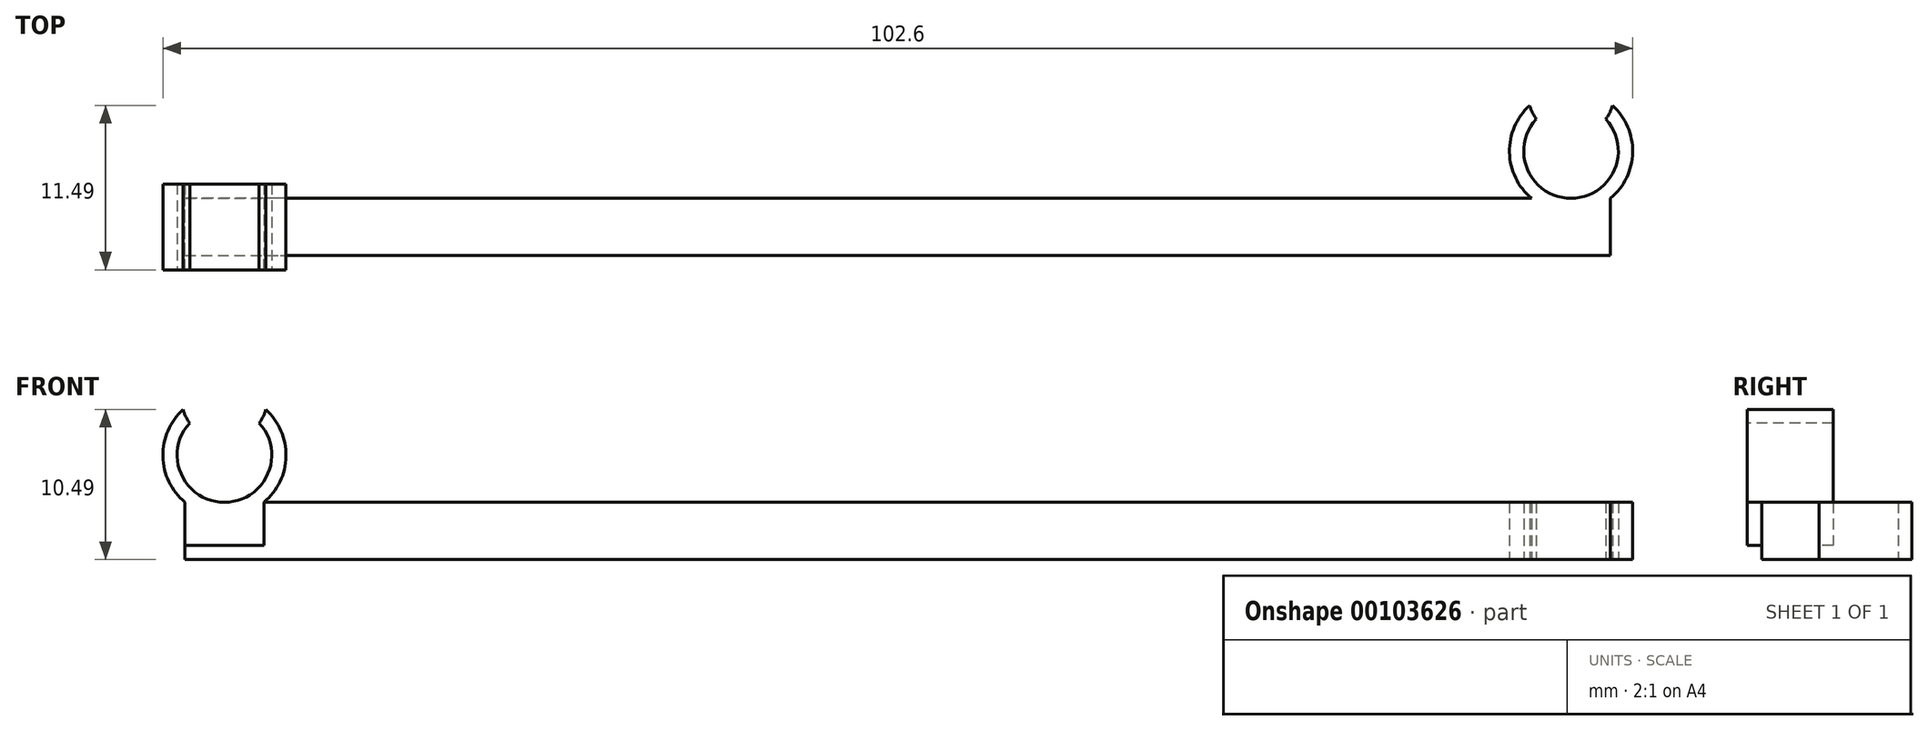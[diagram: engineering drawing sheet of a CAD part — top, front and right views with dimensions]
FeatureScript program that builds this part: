
annotation { "Feature Type Name" : "Feature", "Feature Type Description" : "" }
export const myFeature = defineFeature(function(context is Context, id is Id, definition is map)
    precondition{}
    {
        {
            var Q0;
            Q0=qCreatedBy(makeId("Top.planeOp"),FACE);
            var sketch = newSketch(context, id + "F0", { "sketchPlane" : qUnion([Q0])});
            skArc(sketch, "E0", {"start": v(-2.43, 2.24) * mm, "mid": v(0, -3.3) * mm, "end": v(2.43, 2.24) * mm});
            skArc(sketch, "E1", {"start": v(-2.89, 3.19) * mm, "mid": v(-4.3, -0.09) * mm, "end": v(-2.76, -3.3) * mm});
            skArc(sketch, "E2", {"start": v(-2.89, 3.19) * mm, "mid": v(-2.7, 2.7) * mm, "end": v(-2.43, 2.24) * mm});
            skArc(sketch, "E3.trimOffspring", {"start": v(2.43, 2.24) * mm, "mid": v(2.7, 2.7) * mm, "end": v(2.89, 3.19) * mm});
            skLineSegment(sketch, "E4.bottom", {"start": v(-2.76, -7.3) * mm, "end": v(2.76, -7.3) * mm});
            skLineSegment(sketch, "E4.top", {"start": v(-2.76, -3.3) * mm, "end": v(2.76, -3.3) * mm, "construction": true});
            skLineSegment(sketch, "E4.left", {"start": v(-2.76, -7.3) * mm, "end": v(-2.76, -3.3) * mm});
            skLineSegment(sketch, "E4.right", {"start": v(2.76, -7.3) * mm, "end": v(2.76, -3.3) * mm});
            skArc(sketch, "E5", {"start": v(-2.76, -3.3) * mm, "mid": v(0, -4.3) * mm, "end": v(2.76, -3.3) * mm, "construction": true});
            skArc(sketch, "E6", {"start": v(2.76, -3.3) * mm, "mid": v(4.3, -0.09) * mm, "end": v(2.89, 3.19) * mm});
            skLineSegment(sketch, "E7.bottom", {"start": v(-2.76, -7.3) * mm, "end": v(-96.76, -7.3) * mm});
            skLineSegment(sketch, "E7.top", {"start": v(-2.76, -3.3) * mm, "end": v(-96.76, -3.3) * mm});
            skLineSegment(sketch, "E7.right", {"start": v(-96.76, -7.3) * mm, "end": v(-96.76, -3.3) * mm});
            skSolve(sketch);
        }
        {
            var Q0;
            Q0=qSketchRegion(id+"F0",true);
            extrude(context, id + "F1", {"entities" : qUnion([Q0]), "depth" : 4 * mm});
        }
        {
            var Q0;
            Q0=makeQuery(id+"F1.opExtrude","SWEPT_FACE",FACE,{"disambiguationData":[OSD([sQuery(id+"F0.wireOp",EDGE,"E4.bottom"),sQuery(id+"F0.wireOp",EDGE,"E7.bottom")])]});
            var sketch = newSketch(context, id + "F2", { "sketchPlane" : qUnion([Q0])});
            skArc(sketch, "E8", {"start": v(-96.43, 9.54) * mm, "mid": v(-94, 4) * mm, "end": v(-91.57, 9.54) * mm});
            skArc(sketch, "E9", {"start": v(-96.89, 10.49) * mm, "mid": v(-98.3, 7.21) * mm, "end": v(-96.76, 4) * mm});
            skArc(sketch, "E10", {"start": v(-96.89, 10.49) * mm, "mid": v(-96.7, 10) * mm, "end": v(-96.43, 9.54) * mm});
            skArc(sketch, "E11.trimOffspring", {"start": v(-91.57, 9.54) * mm, "mid": v(-91.3, 10) * mm, "end": v(-91.11, 10.49) * mm});
            skLineSegment(sketch, "E12.bottom", {"start": v(-96.76, 1) * mm, "end": v(-91.24, 1) * mm});
            skLineSegment(sketch, "E12.top", {"start": v(-96.76, 4) * mm, "end": v(-91.24, 4) * mm, "construction": true});
            skLineSegment(sketch, "E12.left", {"start": v(-96.76, 1) * mm, "end": v(-96.76, 4) * mm});
            skLineSegment(sketch, "E12.right", {"start": v(-91.24, 1) * mm, "end": v(-91.24, 4) * mm});
            skArc(sketch, "E13", {"start": v(-96.76, 4) * mm, "mid": v(-94, 3) * mm, "end": v(-91.24, 4) * mm, "construction": true});
            skArc(sketch, "E14", {"start": v(-91.24, 4) * mm, "mid": v(-89.7, 7.21) * mm, "end": v(-91.11, 10.49) * mm});
            skSolve(sketch);
        }
        {
            var Q0;
            Q0 = qSketchRegion(id + "F2", true);
            extrude(context, id + "F3", {"entities" : qUnion([Q0]), "operationType" : NewBodyOperationType.ADD, "oppositeDirection" : true, "depth" : 5 * mm});
        }
        {
            var Q0;
            Q0 = qSketchRegion(id + "F2", true);
            extrude(context, id + "F4", {"entities" : qUnion([Q0]), "operationType" : NewBodyOperationType.ADD, "depth" : 1 * mm});
        }
    });
